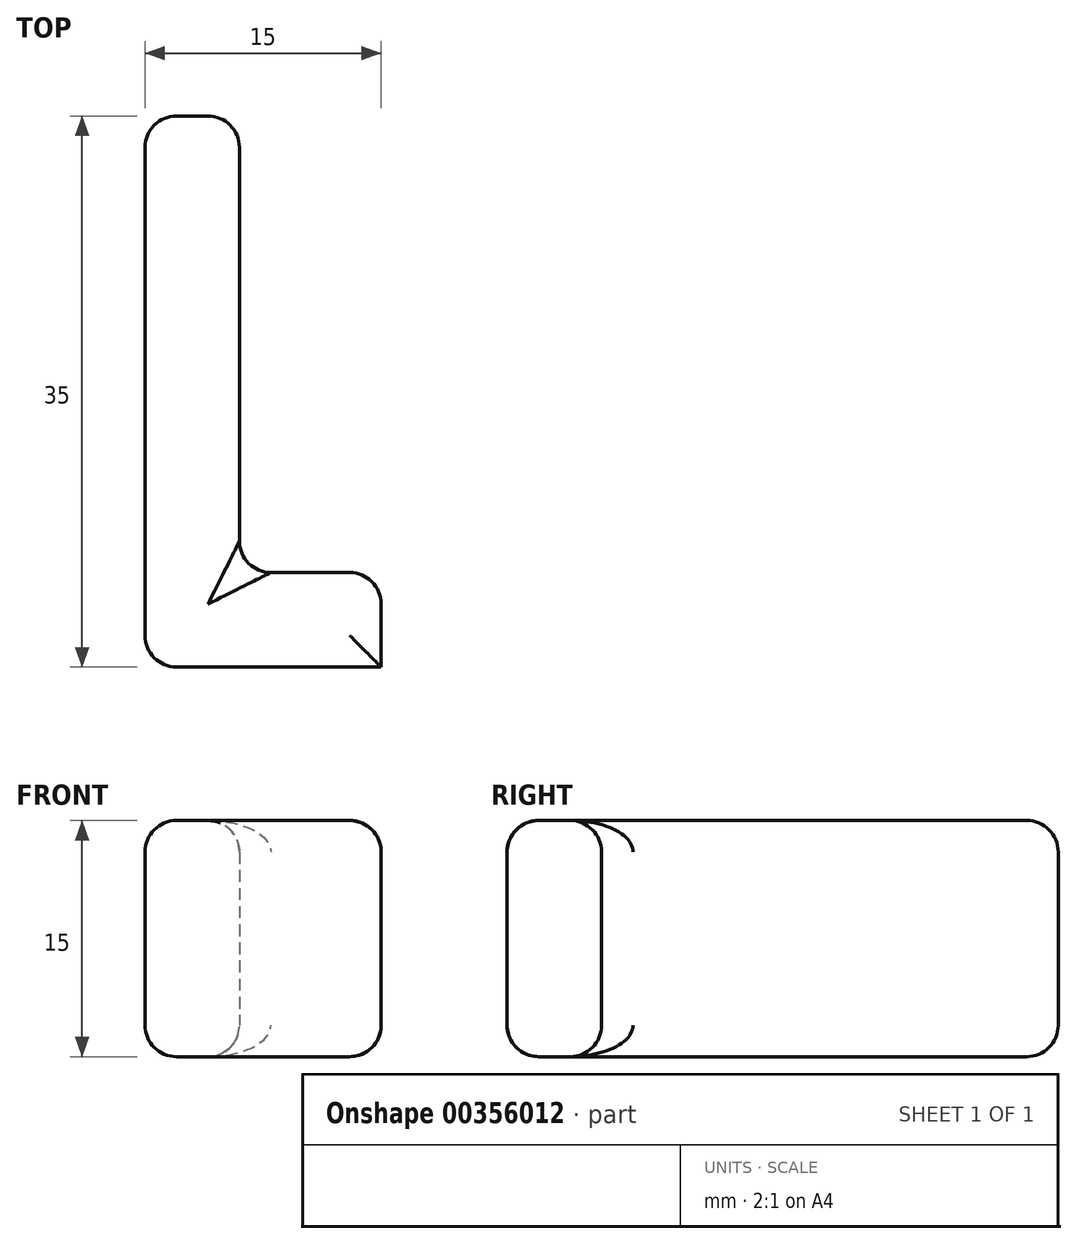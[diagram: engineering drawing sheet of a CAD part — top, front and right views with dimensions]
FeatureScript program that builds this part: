
annotation { "Feature Type Name" : "Feature", "Feature Type Description" : "" }
export const myFeature = defineFeature(function(context is Context, id is Id, definition is map)
    precondition{}
    {
        {
            var Q0;
            Q0=qCreatedBy(makeId("Top.planeOp"),FACE);
            var sketch = newSketch(context, id + "F0", { "sketchPlane" : qUnion([Q0])});
            skLineSegment(sketch, "E0", {"start": v(0, 0) * mm, "end": v(0, 35) * mm});
            skLineSegment(sketch, "E1", {"start": v(0, 0) * mm, "end": v(15, 0) * mm});
            skLineSegment(sketch, "E2", {"start": v(0, 35) * mm, "end": v(6, 35) * mm});
            skLineSegment(sketch, "E3", {"start": v(6, 35) * mm, "end": v(6, 6) * mm});
            skLineSegment(sketch, "E4", {"start": v(6, 6) * mm, "end": v(15, 6) * mm});
            skLineSegment(sketch, "E5", {"start": v(15, 6) * mm, "end": v(15, 0) * mm});
            skSolve(sketch);
        }
        {
            var Q0;
            Q0=makeQuery(id+"F0.imprint","IMPRINT",FACE,{"disambiguationData":[TD([[makeQuery(id+"F0.imprint","IMPRINT",EDGE,{"derivedFrom":sQuery(id+"F0.wireOp",EDGE,"E0")}),-1.0]])]});
            extrude(context, id + "F1", {"entities" : qUnion([Q0]), "depth" : 15 * mm});
        }
        {
            var Q0;
            Q0=makeQuery(id+"F1.opExtrude","CAP_FACE",FACE,{"disambiguationData":[OSD([sQuery(id+"F0.wireOp",EDGE,"E0"),sQuery(id+"F0.wireOp",EDGE,"E1"),sQuery(id+"F0.wireOp",EDGE,"E2"),sQuery(id+"F0.wireOp",EDGE,"E3"),sQuery(id+"F0.wireOp",EDGE,"E4"),sQuery(id+"F0.wireOp",EDGE,"E5")])],"isStart":true});
            var Q1;
            Q1=makeQuery(id+"F1.opExtrude","CAP_FACE",FACE,{"disambiguationData":[OSD([sQuery(id+"F0.wireOp",EDGE,"E0"),sQuery(id+"F0.wireOp",EDGE,"E1"),sQuery(id+"F0.wireOp",EDGE,"E2"),sQuery(id+"F0.wireOp",EDGE,"E3"),sQuery(id+"F0.wireOp",EDGE,"E4"),sQuery(id+"F0.wireOp",EDGE,"E5")])],"isStart":false});
            fillet(context, id + "F2", {"entities" : qUnion([Q0, Q1]), "radius" : 2 * mm, "tangentPropagation" : true, "allowEdgeOverflow" : false});
        }
        {
            var Q0;
            {var subQ0=sQuery(id+"F0.wireOp",EDGE,"E2");Q0=makeQuery(id+"F2.opFillet","BLEND_FACE",FACE,{"disambiguationData":[OSD([subQ0]),TDD([makeQuery(id+"F1.opExtrude","CAP_EDGE",EDGE,{"disambiguationData":[OSD([subQ0])],"isStart":false})])]});}
            var Q1;
            {var subQ0=sQuery(id+"F0.wireOp",EDGE,"E2");Q1=makeQuery(id+"F2.opFillet","BLEND_EDGE",EDGE,{"blendedFrom":[makeQuery(id+"F1.opExtrude","CAP_EDGE",EDGE,{"disambiguationData":[OSD([subQ0])],"isStart":true}),makeQuery(id+"F1.opExtrude","SWEPT_FACE",FACE,{"disambiguationData":[OSD([subQ0])]})],"blendedInto":[makeQuery(id+"F1.opExtrude","SWEPT_FACE",FACE,{"disambiguationData":[OSD([subQ0])]})]});}
            var Q2;
            {var subQ0=sQuery(id+"F0.wireOp",EDGE,"E2");Q2=makeQuery(id+"F2.opFillet","BLEND_FACE",FACE,{"disambiguationData":[OSD([subQ0]),TDD([makeQuery(id+"F1.opExtrude","CAP_EDGE",EDGE,{"disambiguationData":[OSD([subQ0])],"isStart":true})])]});}
            fillet(context, id + "F3", {"entities" : qUnion([Q0, Q1, Q2]), "radius" : 2 * mm, "tangentPropagation" : true, "allowEdgeOverflow" : false});
        }
        {
            var Q0;
            Q0=makeQuery(id+"F1.opExtrude","SWEPT_FACE",FACE,{"disambiguationData":[OSD([sQuery(id+"F0.wireOp",EDGE,"E4")])]});
            var Q1;
            Q1=makeQuery(id+"F1.opExtrude","SWEPT_FACE",FACE,{"disambiguationData":[OSD([sQuery(id+"F0.wireOp",EDGE,"E3")])]});
            var Q2;
            Q2=makeQuery(id+"F1.opExtrude","SWEPT_FACE",FACE,{"disambiguationData":[OSD([sQuery(id+"F0.wireOp",EDGE,"E0")])]});
            fillet(context, id + "F4", {"entities" : qUnion([Q0, Q1, Q2]), "radius" : 2 * mm, "tangentPropagation" : true, "allowEdgeOverflow" : false});
        }
    });
